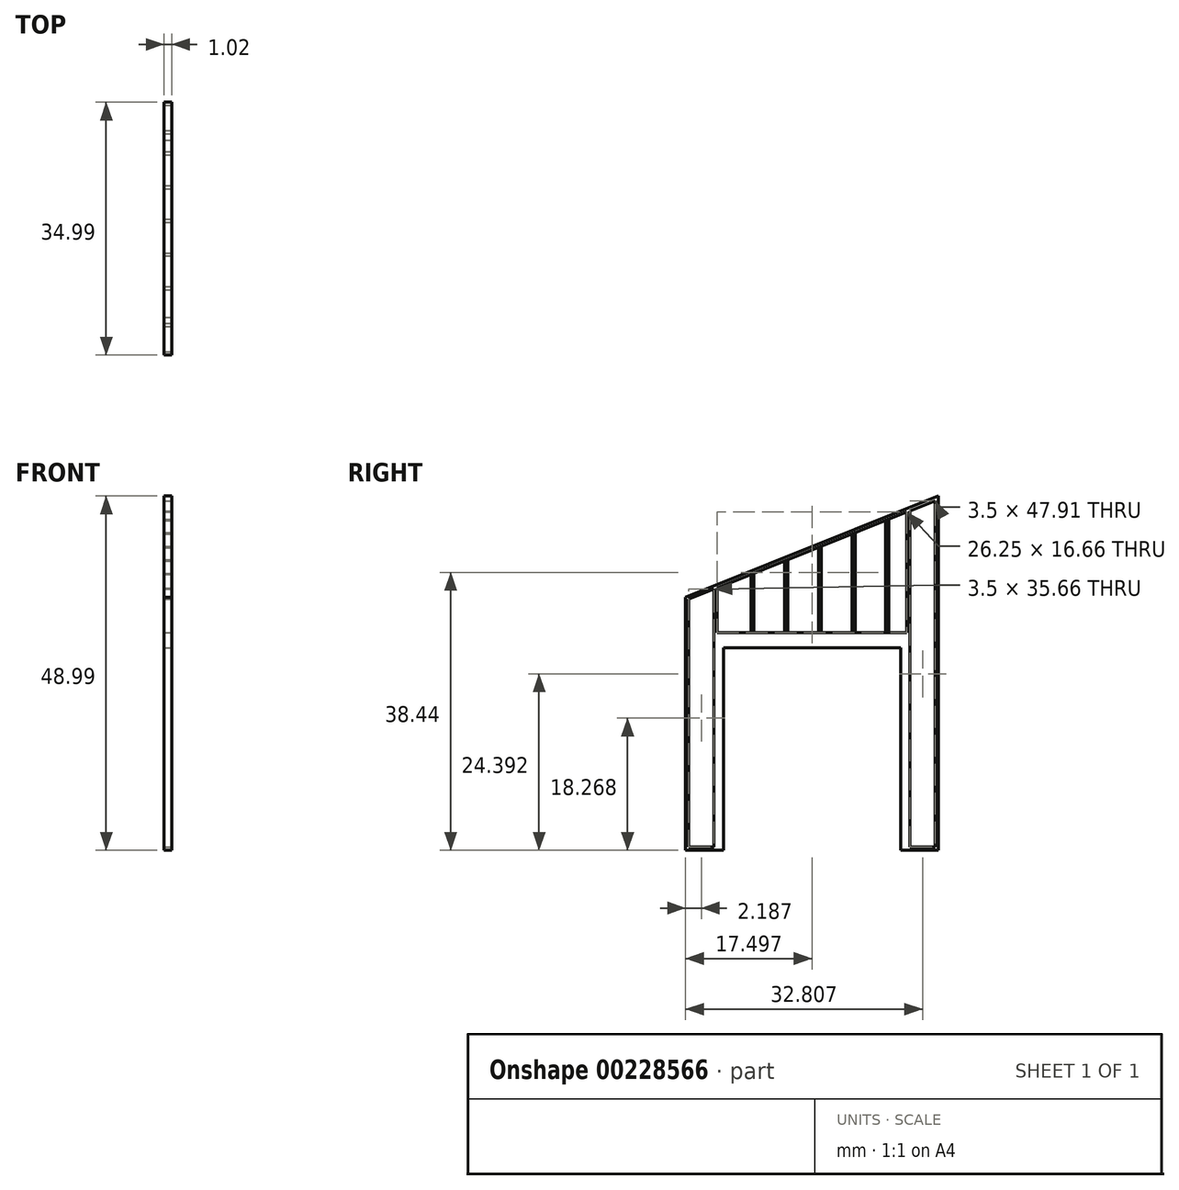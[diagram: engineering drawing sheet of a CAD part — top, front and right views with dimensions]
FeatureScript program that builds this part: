
annotation { "Feature Type Name" : "Feature", "Feature Type Description" : "" }
export const myFeature = defineFeature(function(context is Context, id is Id, definition is map)
    precondition{}
    {
        {
            var Q0;
            Q0=qCreatedBy(makeId("Right.planeOp"),FACE);
            var sketch = newSketch(context, id + "F0", { "sketchPlane" : qUnion([Q0])});
            skLineSegment(sketch, "E0", {"start": v(0, 0) * mm, "end": v(3048, 0) * mm});
            skLineSegment(sketch, "E1", {"start": v(3048, 0) * mm, "end": v(3048, 4267.2) * mm});
            skLineSegment(sketch, "E2", {"start": v(3048, 4267.2) * mm, "end": v(0, 3048) * mm});
            skLineSegment(sketch, "E3", {"start": v(0, 3048) * mm, "end": v(0, 0) * mm});
            skSolve(sketch);
        }
        {
            var Q0;
            Q0=makeQuery(id+"F0.imprint","IMPRINT",FACE,{"disambiguationData":[TD([[makeQuery(id+"F0.imprint","IMPRINT",EDGE,{"derivedFrom":sQuery(id+"F0.wireOp",EDGE,"E0")}),1.0]])]});
            extrude(context, id + "F1", {"entities" : qUnion([Q0]), "depth" : 88.9 * mm});
        }
        {
            var Q0;
            Q0=makeQuery(id+"F1.opExtrude","CAP_FACE",FACE,{"disambiguationData":[OSD([sQuery(id+"F0.wireOp",EDGE,"E0"),sQuery(id+"F0.wireOp",EDGE,"E1"),sQuery(id+"F0.wireOp",EDGE,"E2"),sQuery(id+"F0.wireOp",EDGE,"E3")])],"isStart":false});
            var sketch = newSketch(context, id + "F2", { "sketchPlane" : qUnion([Q0])});
            skLineSegment(sketch, "E4.bottom", {"start": v(457.2, 0) * mm, "end": v(2590.8, 0) * mm});
            skLineSegment(sketch, "E4.top", {"start": v(457.2, 2438.4) * mm, "end": v(2590.8, 2438.4) * mm});
            skLineSegment(sketch, "E4.left", {"start": v(457.2, 0) * mm, "end": v(457.2, 2438.4) * mm});
            skLineSegment(sketch, "E4.right", {"start": v(2590.8, 0) * mm, "end": v(2590.8, 2438.4) * mm});
            skSolve(sketch);
        }
        {
            var Q0;
            Q0=makeQuery(id+"F2.imprint","IMPRINT",FACE,{"disambiguationData":[TD([[makeQuery(id+"F2.imprint","IMPRINT",EDGE,{"derivedFrom":sQuery(id+"F2.wireOp",EDGE,"E4.bottom")}),1.0]])]});
            extrude(context, id + "F3", {"entities" : qUnion([Q0]), "operationType" : NewBodyOperationType.REMOVE, "endBound" : BoundingType.THROUGH_ALL, "oppositeDirection" : true, "depth" : 25.4 * mm});
        }
        {
            var Q0;
            Q0=makeQuery(id+"F1.opExtrude","CAP_FACE",FACE,{"disambiguationData":[OSD([sQuery(id+"F0.wireOp",EDGE,"E0"),sQuery(id+"F0.wireOp",EDGE,"E1"),sQuery(id+"F0.wireOp",EDGE,"E2"),sQuery(id+"F0.wireOp",EDGE,"E3")])],"isStart":false});
            var sketch = newSketch(context, id + "F4", { "sketchPlane" : qUnion([Q0])});
            skLineSegment(sketch, "E5.bottom", {"start": v(342.9, 2438.4) * mm, "end": v(38.1, 2438.4) * mm});
            skLineSegment(sketch, "E5.top", {"start": v(342.9, 0) * mm, "end": v(38.1, 0) * mm});
            skLineSegment(sketch, "E5.left", {"start": v(342.9, 2438.4) * mm, "end": v(342.9, 0) * mm});
            skLineSegment(sketch, "E5.right", {"start": v(38.1, 2438.4) * mm, "end": v(38.1, 0) * mm});
            skLineSegment(sketch, "E6.bottom", {"start": v(3009.9, 0) * mm, "end": v(2705.1, 0) * mm});
            skLineSegment(sketch, "E6.top", {"start": v(3009.9, 2438.4) * mm, "end": v(2705.1, 2438.4) * mm});
            skLineSegment(sketch, "E6.left", {"start": v(3009.9, 0) * mm, "end": v(3009.9, 2438.4) * mm});
            skLineSegment(sketch, "E6.right", {"start": v(2705.1, 0) * mm, "end": v(2705.1, 2438.4) * mm});
            skSolve(sketch);
        }
        {
            var Q0;
            Q0=makeQuery(id+"F4.imprint","IMPRINT",FACE,{"disambiguationData":[TD([[makeQuery(id+"F4.imprint","IMPRINT",EDGE,{"derivedFrom":sQuery(id+"F4.wireOp",EDGE,"E5.bottom")}),1.0]])]});
            var Q1;
            Q1=makeQuery(id+"F4.imprint","IMPRINT",FACE,{"disambiguationData":[TD([[makeQuery(id+"F4.imprint","IMPRINT",EDGE,{"derivedFrom":sQuery(id+"F4.wireOp",EDGE,"E6.bottom")}),1.0]])]});
            extrude(context, id + "F5", {"entities" : qUnion([Q0, Q1]), "operationType" : NewBodyOperationType.REMOVE, "endBound" : BoundingType.THROUGH_ALL, "oppositeDirection" : true, "depth" : 25.4 * mm});
        }
        {
            var Q0;
            Q0=makeQuery(id+"F1.opExtrude","CAP_FACE",FACE,{"disambiguationData":[OSD([sQuery(id+"F0.wireOp",EDGE,"E0"),sQuery(id+"F0.wireOp",EDGE,"E1"),sQuery(id+"F0.wireOp",EDGE,"E2"),sQuery(id+"F0.wireOp",EDGE,"E3")])],"isStart":false});
            var sketch = newSketch(context, id + "F6", { "sketchPlane" : qUnion([Q0])});
            skLineSegment(sketch, "E7", {"start": v(381, 2622.55) * mm, "end": v(381, 3159.37) * mm});
            skLineSegment(sketch, "E8", {"start": v(381, 3159.37) * mm, "end": v(2667, 4073.77) * mm});
            skLineSegment(sketch, "E9", {"start": v(2667, 4073.77) * mm, "end": v(2667, 2622.55) * mm});
            skLineSegment(sketch, "E10", {"start": v(2667, 2622.55) * mm, "end": v(381, 2622.55) * mm});
            skSolve(sketch);
        }
        {
            var Q0;
            Q0=makeQuery(id+"F6.imprint","IMPRINT",FACE,{"disambiguationData":[TD([[makeQuery(id+"F6.imprint","IMPRINT",EDGE,{"derivedFrom":sQuery(id+"F6.wireOp",EDGE,"E7")}),-1.0]])]});
            extrude(context, id + "F7", {"entities" : qUnion([Q0]), "operationType" : NewBodyOperationType.REMOVE, "endBound" : BoundingType.THROUGH_ALL, "oppositeDirection" : true, "depth" : 25.4 * mm});
        }
        {
            var Q0;
            Q0=makeQuery(id+"F1.opExtrude","CAP_FACE",FACE,{"disambiguationData":[OSD([sQuery(id+"F0.wireOp",EDGE,"E0"),sQuery(id+"F0.wireOp",EDGE,"E1"),sQuery(id+"F0.wireOp",EDGE,"E2"),sQuery(id+"F0.wireOp",EDGE,"E3")])],"isStart":false});
            var sketch = newSketch(context, id + "F8", { "sketchPlane" : qUnion([Q0])});
            skLineSegment(sketch, "E11", {"start": v(38.1, 2438.4) * mm, "end": v(38.1, 3022.2) * mm});
            skLineSegment(sketch, "E12", {"start": v(342.9, 2438.4) * mm, "end": v(342.9, 3144.13) * mm});
            skLineSegment(sketch, "E13", {"start": v(342.9, 3144.13) * mm, "end": v(38.1, 3022.2) * mm});
            skLineSegment(sketch, "E14", {"start": v(38.1, 2438.4) * mm, "end": v(342.9, 2438.4) * mm});
            skLineSegment(sketch, "E15", {"start": v(2705.1, 2438.4) * mm, "end": v(2705.1, 4089) * mm});
            skLineSegment(sketch, "E16", {"start": v(3009.9, 2438.4) * mm, "end": v(3009.9, 4210.93) * mm});
            skLineSegment(sketch, "E17", {"start": v(2705.1, 2438.4) * mm, "end": v(3009.9, 2438.4) * mm});
            skLineSegment(sketch, "E18", {"start": v(2705.1, 4089) * mm, "end": v(3009.9, 4210.93) * mm});
            skSolve(sketch);
        }
        {
            var Q0;
            Q0=makeQuery(id+"F8.imprint","IMPRINT",FACE,{"disambiguationData":[TD([[makeQuery(id+"F8.imprint","IMPRINT",EDGE,{"derivedFrom":sQuery(id+"F8.wireOp",EDGE,"E11")}),-1.0]])]});
            var Q1;
            Q1=makeQuery(id+"F8.imprint","IMPRINT",FACE,{"disambiguationData":[TD([[makeQuery(id+"F8.imprint","IMPRINT",EDGE,{"derivedFrom":sQuery(id+"F8.wireOp",EDGE,"E15")}),-1.0]])]});
            extrude(context, id + "F9", {"entities" : qUnion([Q0, Q1]), "operationType" : NewBodyOperationType.REMOVE, "endBound" : BoundingType.THROUGH_ALL, "oppositeDirection" : true, "depth" : 25.4 * mm});
        }
        {
            var Q0;
            Q0=makeQuery(id+"F1.opExtrude","CAP_FACE",FACE,{"disambiguationData":[OSD([sQuery(id+"F0.wireOp",EDGE,"E0"),sQuery(id+"F0.wireOp",EDGE,"E1"),sQuery(id+"F0.wireOp",EDGE,"E2"),sQuery(id+"F0.wireOp",EDGE,"E3")])],"isStart":false});
            var sketch = newSketch(context, id + "F10", { "sketchPlane" : qUnion([Q0])});
            skLineSegment(sketch, "E19", {"start": v(787.4, 3321.93) * mm, "end": v(787.4, 2622.55) * mm});
            skLineSegment(sketch, "E20", {"start": v(787.4, 2622.55) * mm, "end": v(825.5, 2622.55) * mm});
            skLineSegment(sketch, "E21", {"start": v(825.5, 2622.55) * mm, "end": v(825.5, 3337.17) * mm});
            skLineSegment(sketch, "E22", {"start": v(825.5, 3337.17) * mm, "end": v(787.4, 3321.93) * mm});
            skLineSegment(sketch, "E23", {"start": v(1193.8, 3484.49) * mm, "end": v(1193.8, 2622.55) * mm});
            skLineSegment(sketch, "E24", {"start": v(1193.8, 2622.55) * mm, "end": v(1231.9, 2622.55) * mm});
            skLineSegment(sketch, "E25", {"start": v(1231.9, 2622.55) * mm, "end": v(1231.9, 3499.73) * mm});
            skLineSegment(sketch, "E26", {"start": v(1231.9, 3499.73) * mm, "end": v(1193.8, 3484.49) * mm});
            skLineSegment(sketch, "E27", {"start": v(1600.2, 3647.05) * mm, "end": v(1600.2, 2622.55) * mm});
            skLineSegment(sketch, "E28", {"start": v(1600.2, 2622.55) * mm, "end": v(1638.3, 2622.55) * mm});
            skLineSegment(sketch, "E29", {"start": v(1638.3, 2622.55) * mm, "end": v(1638.3, 3662.29) * mm});
            skLineSegment(sketch, "E30", {"start": v(1638.3, 3662.29) * mm, "end": v(1600.2, 3647.05) * mm});
            skLineSegment(sketch, "E31", {"start": v(2006.6, 3809.6) * mm, "end": v(2006.6, 2622.55) * mm});
            skLineSegment(sketch, "E32", {"start": v(2006.6, 2622.55) * mm, "end": v(2044.7, 2622.55) * mm});
            skLineSegment(sketch, "E33", {"start": v(2044.7, 2622.55) * mm, "end": v(2044.7, 3824.85) * mm});
            skLineSegment(sketch, "E34", {"start": v(2044.7, 3824.85) * mm, "end": v(2006.6, 3809.6) * mm});
            skLineSegment(sketch, "E35", {"start": v(2413, 3972.17) * mm, "end": v(2413, 2622.55) * mm});
            skLineSegment(sketch, "E36", {"start": v(2413, 2622.55) * mm, "end": v(2451.1, 2622.55) * mm});
            skLineSegment(sketch, "E37", {"start": v(2451.1, 2622.55) * mm, "end": v(2451.1, 3987.4) * mm});
            skLineSegment(sketch, "E38", {"start": v(2451.1, 3987.4) * mm, "end": v(2413, 3972.17) * mm});
            skSolve(sketch);
        }
        {
            var Q0;
            Q0=makeQuery(id+"F10.imprint","IMPRINT",FACE,{"disambiguationData":[TD([[makeQuery(id+"F10.imprint","IMPRINT",EDGE,{"derivedFrom":sQuery(id+"F10.wireOp",EDGE,"E19")}),1.0]])]});
            var Q1;
            Q1=makeQuery(id+"F10.imprint","IMPRINT",FACE,{"disambiguationData":[TD([[makeQuery(id+"F10.imprint","IMPRINT",EDGE,{"derivedFrom":sQuery(id+"F10.wireOp",EDGE,"E23")}),1.0]])]});
            var Q2;
            Q2=makeQuery(id+"F10.imprint","IMPRINT",FACE,{"disambiguationData":[TD([[makeQuery(id+"F10.imprint","IMPRINT",EDGE,{"derivedFrom":sQuery(id+"F10.wireOp",EDGE,"E27")}),1.0]])]});
            var Q3;
            Q3=makeQuery(id+"F10.imprint","IMPRINT",FACE,{"disambiguationData":[TD([[makeQuery(id+"F10.imprint","IMPRINT",EDGE,{"derivedFrom":sQuery(id+"F10.wireOp",EDGE,"E31")}),1.0]])]});
            var Q4;
            Q4=makeQuery(id+"F10.imprint","IMPRINT",FACE,{"disambiguationData":[TD([[makeQuery(id+"F10.imprint","IMPRINT",EDGE,{"derivedFrom":sQuery(id+"F10.wireOp",EDGE,"E35")}),1.0]])]});
            extrude(context, id + "F11", {"entities" : qUnion([Q0, Q1, Q2, Q3, Q4]), "oppositeDirection" : true, "depth" : 88.9 * mm});
        }
        {
            var Q0;
            Q0=makeQuery(id+"F1.opExtrude","CAP_FACE",FACE,{"disambiguationData":[OSD([sQuery(id+"F0.wireOp",EDGE,"E0"),sQuery(id+"F0.wireOp",EDGE,"E1"),sQuery(id+"F0.wireOp",EDGE,"E2"),sQuery(id+"F0.wireOp",EDGE,"E3")])],"isStart":false});
            var sketch = newSketch(context, id + "F12", { "sketchPlane" : qUnion([Q0])});
            skLineSegment(sketch, "E39.bottom", {"start": v(38.1, 0) * mm, "end": v(342.9, 0) * mm});
            skLineSegment(sketch, "E39.top", {"start": v(38.1, 38.1) * mm, "end": v(342.9, 38.1) * mm});
            skLineSegment(sketch, "E39.left", {"start": v(38.1, 0) * mm, "end": v(38.1, 38.1) * mm});
            skLineSegment(sketch, "E39.right", {"start": v(342.9, 0) * mm, "end": v(342.9, 38.1) * mm});
            skLineSegment(sketch, "E40.bottom", {"start": v(2705.1, 0) * mm, "end": v(3009.9, 0) * mm});
            skLineSegment(sketch, "E40.top", {"start": v(2705.1, 38.1) * mm, "end": v(3009.9, 38.1) * mm});
            skLineSegment(sketch, "E40.left", {"start": v(2705.1, 0) * mm, "end": v(2705.1, 38.1) * mm});
            skLineSegment(sketch, "E40.right", {"start": v(3009.9, 0) * mm, "end": v(3009.9, 38.1) * mm});
            skSolve(sketch);
        }
        {
            var Q0;
            Q0=makeQuery(id+"F12.imprint","IMPRINT",FACE,{"disambiguationData":[TD([[makeQuery(id+"F12.imprint","IMPRINT",EDGE,{"derivedFrom":sQuery(id+"F12.wireOp",EDGE,"E39.bottom")}),1.0]])]});
            var Q1;
            Q1=makeQuery(id+"F12.imprint","IMPRINT",FACE,{"disambiguationData":[TD([[makeQuery(id+"F12.imprint","IMPRINT",EDGE,{"derivedFrom":sQuery(id+"F12.wireOp",EDGE,"E40.bottom")}),1.0]])]});
            extrude(context, id + "F13", {"entities" : qUnion([Q0, Q1]), "operationType" : NewBodyOperationType.ADD, "oppositeDirection" : true, "depth" : 88.9 * mm});
        }
        {
            var Q0;
            Q0=makeQuery(id+"F11.opExtrude","SWEPT_BODY",BODY,{"disambiguationData":[OSD([sQuery(id+"F10.wireOp",EDGE,"E35"),sQuery(id+"F10.wireOp",EDGE,"E36"),sQuery(id+"F10.wireOp",EDGE,"E37"),sQuery(id+"F10.wireOp",EDGE,"E38")])]});
            var Q1;
            Q1=makeQuery(id+"F11.opExtrude","SWEPT_BODY",BODY,{"disambiguationData":[OSD([sQuery(id+"F10.wireOp",EDGE,"E27"),sQuery(id+"F10.wireOp",EDGE,"E28"),sQuery(id+"F10.wireOp",EDGE,"E29"),sQuery(id+"F10.wireOp",EDGE,"E30")])]});
            var Q2;
            Q2=makeQuery(id+"F11.opExtrude","SWEPT_BODY",BODY,{"disambiguationData":[OSD([sQuery(id+"F10.wireOp",EDGE,"E19"),sQuery(id+"F10.wireOp",EDGE,"E20"),sQuery(id+"F10.wireOp",EDGE,"E21"),sQuery(id+"F10.wireOp",EDGE,"E22")])]});
            var Q3;
            Q3=makeQuery(id+"F1.opExtrude","SWEPT_BODY",BODY,{"disambiguationData":[OSD([sQuery(id+"F0.wireOp",EDGE,"E0"),sQuery(id+"F0.wireOp",EDGE,"E1"),sQuery(id+"F0.wireOp",EDGE,"E2"),sQuery(id+"F0.wireOp",EDGE,"E3")])]});
            var Q4;
            Q4=makeQuery(id+"F11.opExtrude","SWEPT_BODY",BODY,{"disambiguationData":[OSD([sQuery(id+"F10.wireOp",EDGE,"E23"),sQuery(id+"F10.wireOp",EDGE,"E24"),sQuery(id+"F10.wireOp",EDGE,"E25"),sQuery(id+"F10.wireOp",EDGE,"E26")])]});
            var Q5;
            Q5=makeQuery(id+"F11.opExtrude","SWEPT_BODY",BODY,{"disambiguationData":[OSD([sQuery(id+"F10.wireOp",EDGE,"E31"),sQuery(id+"F10.wireOp",EDGE,"E32"),sQuery(id+"F10.wireOp",EDGE,"E33"),sQuery(id+"F10.wireOp",EDGE,"E34")])]});
            var Q6;
            Q6=qCreatedBy(makeId("Origin.pointOp"),VERTEX);
            transform(context, id + "F14", {"entities" : qUnion([Q0, Q1, Q2, Q3, Q4, Q5]), "transformType" : TransformType.SCALE_UNIFORMLY, "scale" : 1 / 87.1, "scalePoint" : qUnion([Q6]), "makeCopy" : false});
        }
    });
